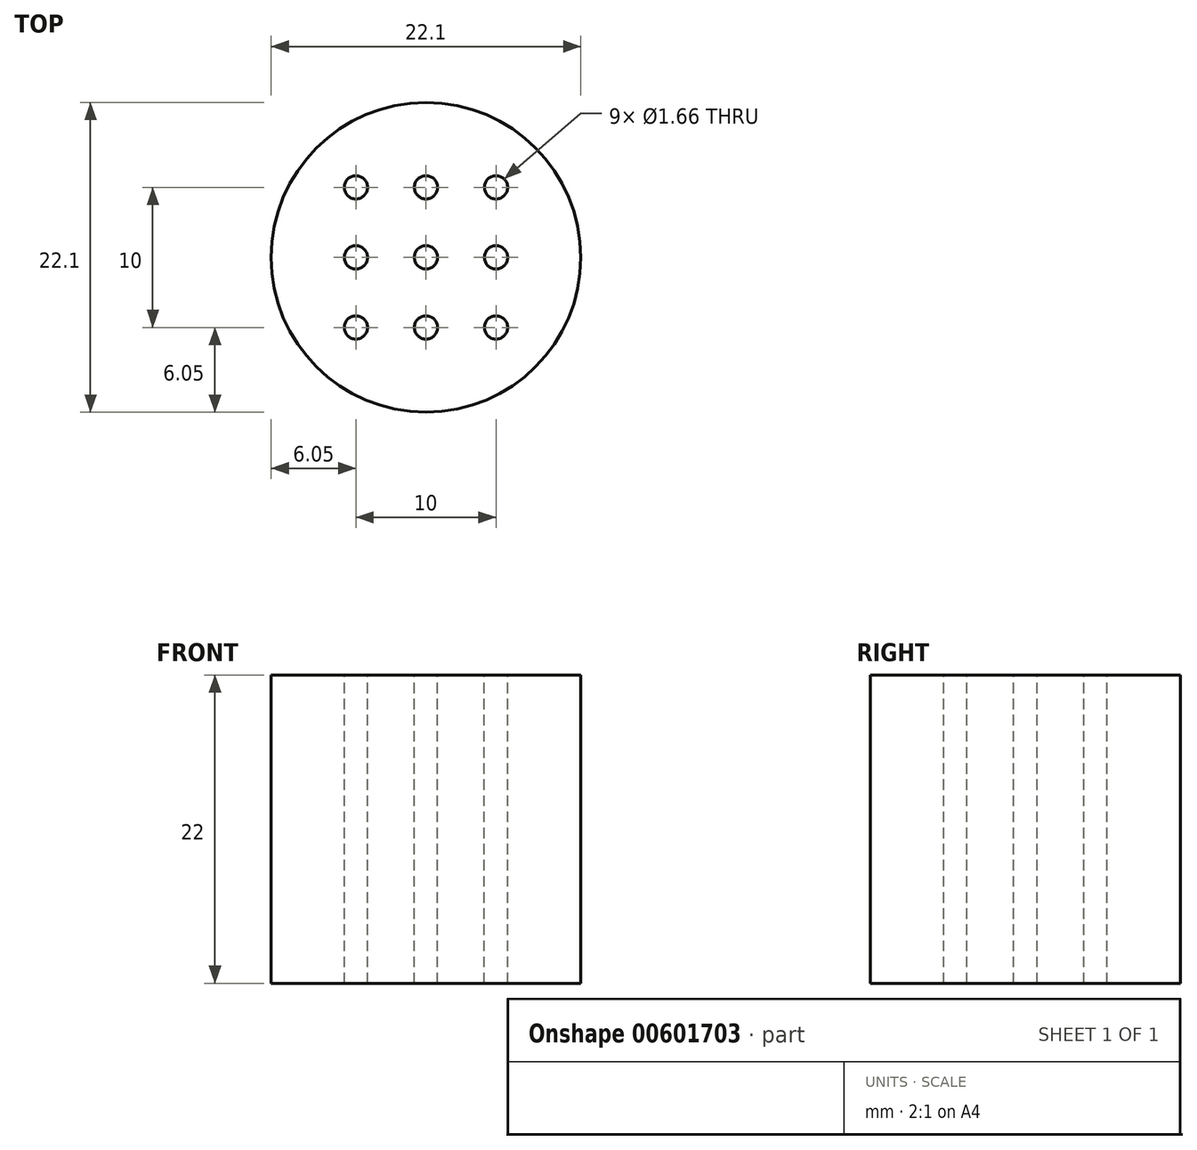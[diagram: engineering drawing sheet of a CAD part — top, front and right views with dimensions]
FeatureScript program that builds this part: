
annotation { "Feature Type Name" : "Feature", "Feature Type Description" : "" }
export const myFeature = defineFeature(function(context is Context, id is Id, definition is map)
    precondition{}
    {
        {
            var Q0;
            Q0=qCreatedBy(makeId("Top.planeOp"),FACE);
            var sketch = newSketch(context, id + "F0", { "sketchPlane" : qUnion([Q0])});
            skCircle(sketch, "E0", {"center": v(0, 0) * mm, "radius": 11.05 * mm});
            skPoint(sketch, "E1", {"position": v(0, 5) * mm});
            skPoint(sketch, "E2", {"position": v(5, 5) * mm});
            skPoint(sketch, "E3", {"position": v(5, 0) * mm});
            skPoint(sketch, "E4", {"position": v(5, -5) * mm});
            skPoint(sketch, "E5", {"position": v(0, -5) * mm});
            skPoint(sketch, "E6", {"position": v(-5, -5) * mm});
            skPoint(sketch, "E7", {"position": v(-5, 0) * mm});
            skPoint(sketch, "E8", {"position": v(-5, 5) * mm});
            skSolve(sketch);
        }
        {
            var Q0;
            Q0=makeQuery(id+"F0.imprint","IMPRINT",FACE,{"disambiguationData":[TD([[makeQuery(id+"F0.imprint","IMPRINT",EDGE,{"derivedFrom":sQuery(id+"F0.wireOp",EDGE,"E0")}),1.0]])]});
            var Q1;
            Q1=sQuery(id+"F0.wireOp",EDGE,"E0");
            extrude(context, id + "F1", {"entities" : qUnion([Q0]), "surfaceEntities" : qUnion([Q1]), "oppositeDirection" : true, "depth" : 22 * mm, "offsetDistance" : 25.4 * mm});
        }
        {
            var Q0;
            Q0=sQuery(id+"F0.wireOp",VERTEX,"E1");
            var Q1;
            Q1=sQuery(id+"F0.wireOp",VERTEX,"E8");
            var Q2;
            Q2=sQuery(id+"F0.wireOp",VERTEX,"E7");
            var Q3;
            Q3=sQuery(id+"F0.wireOp",VERTEX,"E6");
            var Q4;
            Q4=sQuery(id+"F0.wireOp",VERTEX,"E5");
            var Q5;
            Q5=sQuery(id+"F0.wireOp",VERTEX,"E4");
            var Q6;
            Q6=sQuery(id+"F0.wireOp",VERTEX,"E3");
            var Q7;
            Q7=sQuery(id+"F0.wireOp",VERTEX,"E2");
            var Q8;
            Q8=sQuery(id+"F0.wireOp",VERTEX,"E0.center");
            var Q9;
            Q9=makeQuery(id+"F1.opExtrude","SWEPT_BODY",BODY,{"disambiguationData":[OSD([sQuery(id+"F0.wireOp",EDGE,"E0")])]});
            hole(context, id + "F2", {"style" : HoleStyle.SIMPLE, "endStyle" : HoleEndStyle.THROUGH, "holeDiameter" : 1.66 * mm, "majorDiameter" : 6.35 * mm, "isTappedThrough" : true, "tappedDepth" : 12.7 * mm, "tapClearance" : 3, "locations" : qUnion([Q0, Q1, Q2, Q3, Q4, Q5, Q6, Q7, Q8]), "scope" : qUnion([Q9])});
        }
    });
